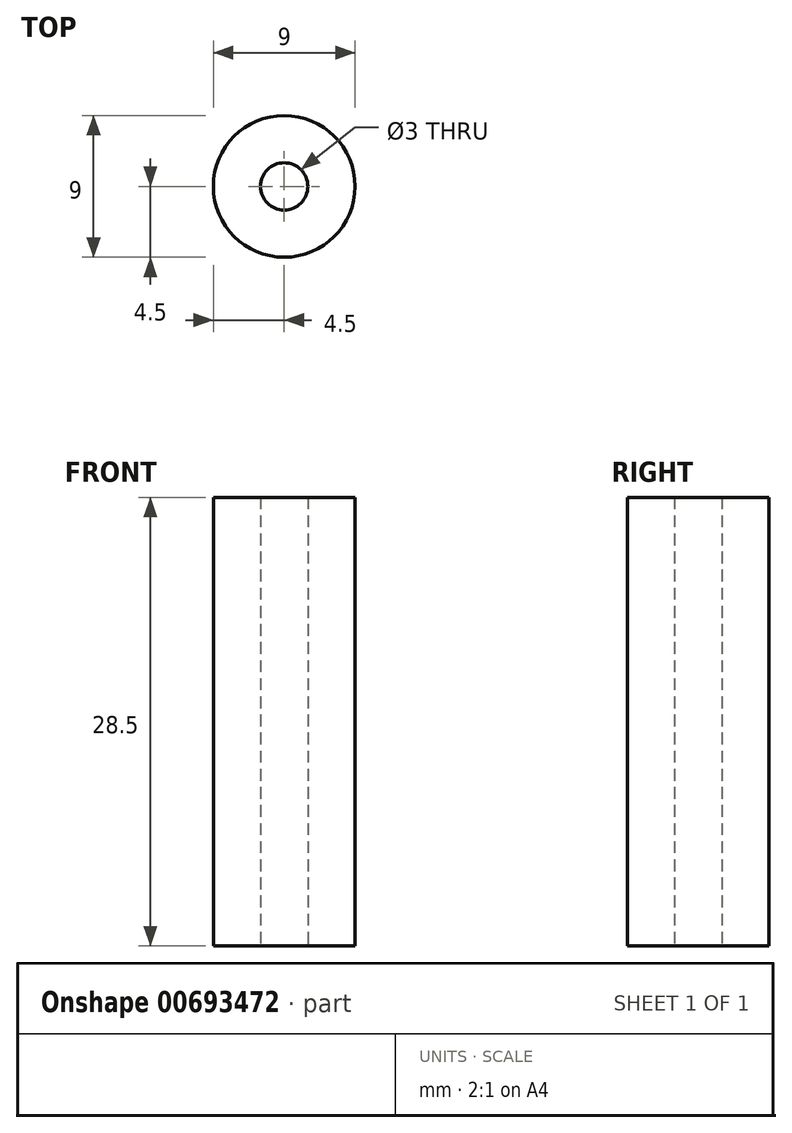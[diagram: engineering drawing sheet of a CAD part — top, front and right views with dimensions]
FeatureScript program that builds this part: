
annotation { "Feature Type Name" : "Feature", "Feature Type Description" : "" }
export const myFeature = defineFeature(function(context is Context, id is Id, definition is map)
    precondition{}
    {
        {
            var Q0;
            Q0=qCreatedBy(makeId("Top.planeOp"),FACE);
            var sketch = newSketch(context, id + "F0", { "sketchPlane" : qUnion([Q0])});
            skCircle(sketch, "E0", {"center": v(0, 0) * mm, "radius": 4.5 * mm});
            skCircle(sketch, "E1", {"center": v(0, 0) * mm, "radius": 1.5 * mm});
            skSolve(sketch);
        }
        {
            var Q0;
            Q0 = qSketchRegion(id + "F0", true);
            extrude(context, id + "F1", {"entities" : qUnion([Q0]), "depth" : 28.5 * mm, "offsetDistance" : 25.4 * mm});
        }
    });
